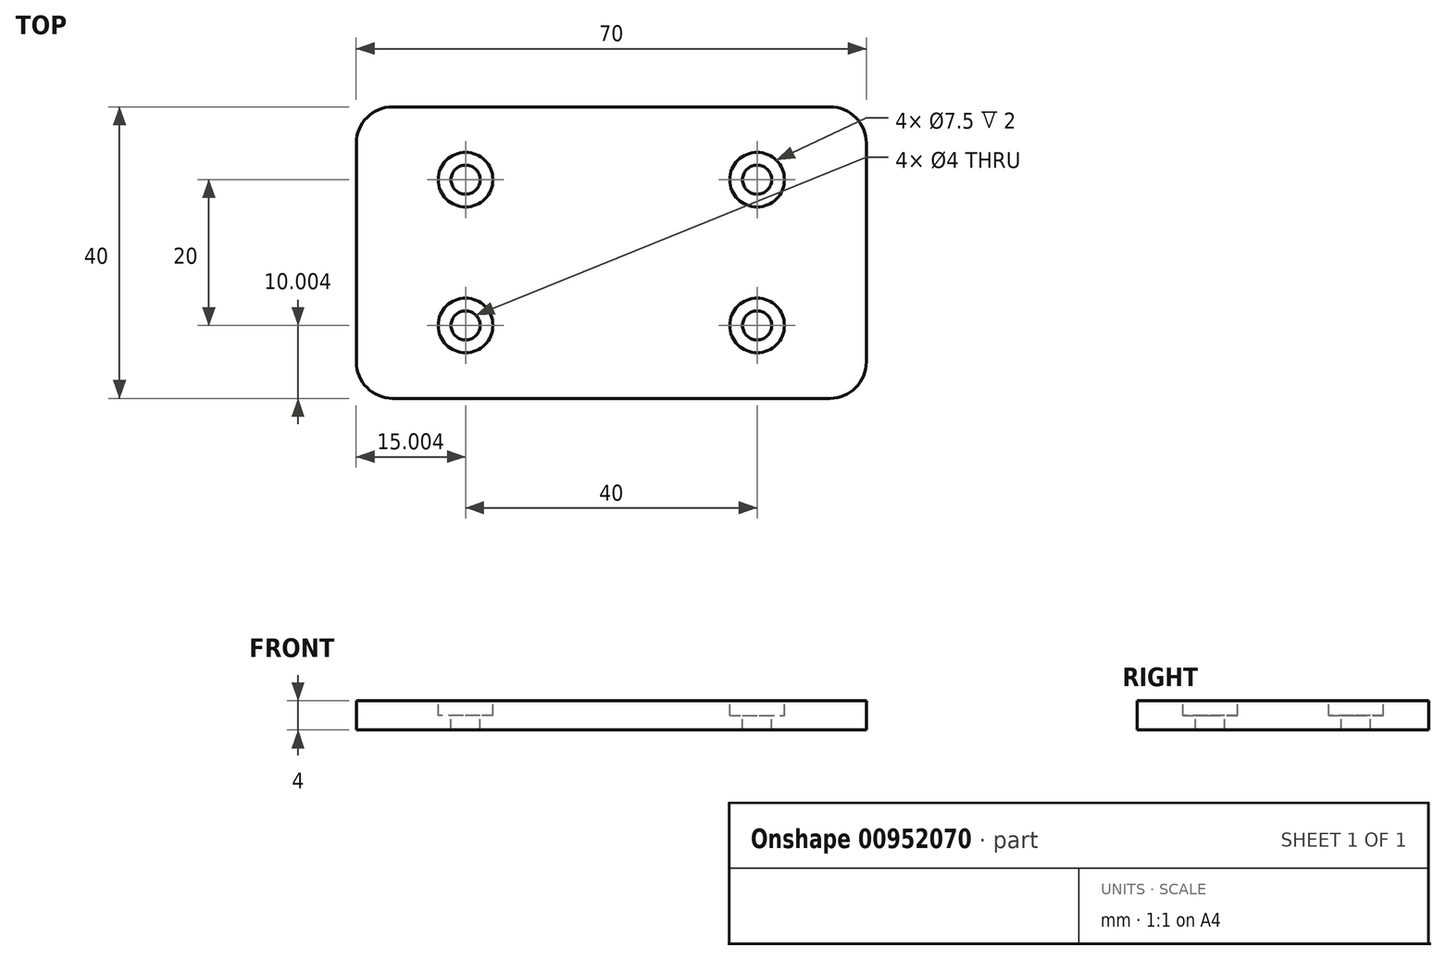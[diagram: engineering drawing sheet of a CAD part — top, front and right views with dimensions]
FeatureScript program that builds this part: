
annotation { "Feature Type Name" : "Feature", "Feature Type Description" : "" }
export const myFeature = defineFeature(function(context is Context, id is Id, definition is map)
    precondition{}
    {
        {
            var Q0;
            Q0=qCreatedBy(makeId("Top.planeOp"),FACE);
            var sketch = newSketch(context, id + "F0", { "sketchPlane" : qUnion([Q0])});
            skLineSegment(sketch, "E0.bottom", {"start": v(-32.52, 25.06) * mm, "end": v(2.48, 25.06) * mm});
            skLineSegment(sketch, "E0.top", {"start": v(-32.52, -14.94) * mm, "end": v(2.48, -14.94) * mm});
            skLineSegment(sketch, "E0.left", {"start": v(-32.52, 25.06) * mm, "end": v(-32.52, -14.94) * mm});
            skLineSegment(sketch, "E0.right", {"start": v(2.48, 25.06) * mm, "end": v(2.48, -14.94) * mm});
            skSolve(sketch);
        }
        {
            var Q0;
            Q0=makeQuery(id+"F0.imprint","IMPRINT",FACE,{"disambiguationData":[TD([[makeQuery(id+"F0.imprint","IMPRINT",EDGE,{"derivedFrom":sQuery(id+"F0.wireOp",EDGE,"E0.bottom")}),-1.0]])]});
            extrude(context, id + "F1", {"entities" : qUnion([Q0]), "depth" : 4 * mm, "offsetDistance" : 25 * mm});
        }
        {
            var Q0;
            Q0=makeQuery(id+"F1.opExtrude","SWEPT_EDGE",EDGE,{"disambiguationData":[OSD([sQuery(id+"F0.wireOp",EDGE,"E0.bottom"),sQuery(id+"F0.wireOp",EDGE,"E0.left")])]});
            var Q1;
            Q1=makeQuery(id+"F1.opExtrude","SWEPT_EDGE",EDGE,{"disambiguationData":[OSD([sQuery(id+"F0.wireOp",EDGE,"E0.top"),sQuery(id+"F0.wireOp",EDGE,"E0.left")])]});
            fillet(context, id + "F2", {"entities" : qUnion([Q0, Q1]), "radius" : 5 * mm, "tangentPropagation" : true, "allowEdgeOverflow" : false});
        }
        {
            var Q0;
            Q0=makeQuery(id+"F1.opExtrude","CAP_FACE",FACE,{"disambiguationData":[OSD([sQuery(id+"F0.wireOp",EDGE,"E0.bottom"),sQuery(id+"F0.wireOp",EDGE,"E0.top"),sQuery(id+"F0.wireOp",EDGE,"E0.left"),sQuery(id+"F0.wireOp",EDGE,"E0.right")])],"isStart":false});
            var sketch = newSketch(context, id + "F3", { "sketchPlane" : qUnion([Q0])});
            skCircle(sketch, "E1", {"center": v(-17.52, 15.06) * mm, "radius": 3.75 * mm});
            skCircle(sketch, "E2", {"center": v(-17.52, -4.94) * mm, "radius": 3.75 * mm});
            skSolve(sketch);
        }
        {
            var Q0;
            Q0=makeQuery(id+"F3.imprint","IMPRINT",FACE,{"disambiguationData":[TD([[makeQuery(id+"F3.imprint","IMPRINT",EDGE,{"derivedFrom":sQuery(id+"F3.wireOp",EDGE,"E2")}),1.0]])]});
            var Q1;
            Q1=makeQuery(id+"F3.imprint","IMPRINT",FACE,{"disambiguationData":[TD([[makeQuery(id+"F3.imprint","IMPRINT",EDGE,{"derivedFrom":sQuery(id+"F3.wireOp",EDGE,"E1")}),1.0]])]});
            extrude(context, id + "F4", {"entities" : qUnion([Q0, Q1]), "operationType" : NewBodyOperationType.REMOVE, "depth" : -2 * mm, "offsetDistance" : 25 * mm});
        }
        {
            var Q0;
            Q0=makeQuery(id+"F4.boolean.opBoolean","COPY",FACE,{"derivedFrom":makeQuery(id+"F4.opExtrude","CAP_FACE",FACE,{"disambiguationData":[OSD([sQuery(id+"F3.wireOp",EDGE,"E1")])],"isStart":false})});
            var sketch = newSketch(context, id + "F5", { "sketchPlane" : qUnion([Q0])});
            skCircle(sketch, "E3", {"center": v(-17.52, 15.06) * mm, "radius": 2 * mm});
            skSolve(sketch);
        }
        {
            var Q0;
            Q0=makeQuery(id+"F5.imprint","IMPRINT",FACE,{"disambiguationData":[TD([[makeQuery(id+"F5.imprint","IMPRINT",EDGE,{"derivedFrom":sQuery(id+"F5.wireOp",EDGE,"E3")}),1.0]])]});
            extrude(context, id + "F6", {"entities" : qUnion([Q0]), "operationType" : NewBodyOperationType.REMOVE, "oppositeDirection" : true, "depth" : 5 * mm, "offsetDistance" : 25 * mm});
        }
        {
            var Q0;
            Q0=makeQuery(id+"F4.boolean.opBoolean","COPY",FACE,{"derivedFrom":makeQuery(id+"F4.opExtrude","CAP_FACE",FACE,{"disambiguationData":[OSD([sQuery(id+"F3.wireOp",EDGE,"E2")])],"isStart":false})});
            var sketch = newSketch(context, id + "F7", { "sketchPlane" : qUnion([Q0])});
            skCircle(sketch, "E4", {"center": v(-17.52, -4.94) * mm, "radius": 2 * mm});
            skSolve(sketch);
        }
        {
            var Q0;
            Q0=makeQuery(id+"F7.imprint","IMPRINT",FACE,{"disambiguationData":[TD([[makeQuery(id+"F7.imprint","IMPRINT",EDGE,{"derivedFrom":sQuery(id+"F7.wireOp",EDGE,"E4")}),1.0]])]});
            extrude(context, id + "F8", {"entities" : qUnion([Q0]), "operationType" : NewBodyOperationType.REMOVE, "oppositeDirection" : true, "depth" : 5 * mm, "offsetDistance" : 25 * mm});
        }
        {
            var Q0;
            Q0=makeQuery(id+"F1.opExtrude","SWEPT_BODY",BODY,{"disambiguationData":[OSD([sQuery(id+"F0.wireOp",EDGE,"E0.bottom"),sQuery(id+"F0.wireOp",EDGE,"E0.top"),sQuery(id+"F0.wireOp",EDGE,"E0.left"),sQuery(id+"F0.wireOp",EDGE,"E0.right")])]});
            var Q1;
            Q1=makeQuery(id+"F1.opExtrude","SWEPT_FACE",FACE,{"disambiguationData":[OSD([sQuery(id+"F0.wireOp",EDGE,"E0.right")])]});
            mirror(context, id + "F9", {"operationType" : NewBodyOperationType.ADD, "entities" : qUnion([Q0]), "mirrorPlane" : qUnion([Q1])});
        }
    });
